# Revit family: Electronics_Expansion-Inputs_Biamp_Vocia_8-Channel-Live-Audio-Input-Device_VI-8__
name_source: partatom
category: Communication Devices
units: mm (PartAtom-declared; Revit-internal decimal feet)

## family parameters
Cut with Voids When Loaded = No
Host = Face
Maintain Annotation Orientation = No
OmniClass Number = 23.85.10.11.14
OmniClass Title = Audio Equipment
Part Type = Normal
Room Calculation Point = No
Round Connector Dimension = Use Diameter
Shared = No

## types (1)
- VI-8
    A/D Converters = 24-bit
    Altitude = 0-10,000 ft (0-3000m) MSL
    Apparent Load = 35 VA
    Compliance = FCC Part 15B (USA); CE marked (Europe); RCM (Australia); EAC (Eurasian Customs Union); RoHS Directive (Europe)
    Connector Description = 24V DC; <100mV Ripple (Max 35W)
    Crosstalk = 10kHz: < -75dB
    Current Limit = 0.8A
    DC Input = 24V DC; <100mV Ripple (Max 35W)
    DC Reference Output = 24V; 100mA limited
    Default Elevation = 4' - 0"
    Depth = 0' - 10"
    Description = Vocia® VI-8 8-Channel Live Audio Input Device
    Dynamic Range = >100dB
    Equivalent Input Noise = < -125dBu
    Frequency Response = 20Hz~20kHz: +0, -1dB
    Height = 0' - 1 1/2"
    High Range Logic High = 12-30V DC
    High Range Logic Low = 0-8V DC
    Housing Material = Biamp - Metal - Silver
    Humidity = 0-95% relative humidity (non-condensing)
    Input Impedance = 8kOhm
    Input Isolation = 500V RMS
    Input Transient Protection = ± 8kV Peak
    Manufacturer = Biamp
    Max Continuous Current = 0.35A
    Max Input Level = 24dBu
    Max Operating Voltage = 125VAC, 60VDC / 35V
    Max Power Consumption = 35 W
    Max Switching Capacity = 37VA
    Min Operating Load = 10μA at 10mV DC
    Model = Vocia VI-8
    Network Audio = 20-bits, 48kHz, 5-1/3ms (fixed)
    Network Connection = Dual RJ45 with shielded Ethernet (CAT5, CAT5e, CAT6, or CAT7)
    Number of Poles = 1
    Power Factor = 1
    Product Documentation Link = https://downloads.biamp.com
    Product Page URL = https://www.biamp.com
    Product data url = https://www.bimobject.com
    Quantity Control Inputs = 9
    Quantity Control Outputs = 4
    Sample Rate = 48kHz
    Status Out Type = FET Switch, open drain (low side driver)
    THD+N = 20Hz~20kHz: <0.05%
    TTL Logic High = 2-5V
    TTL Logic Low = 0–0.8V
    Temperature Range = 18 - 108° F (-8 – 42° C)
    Type Control Outputs = Form C Voltage free change over contact
    URL = https://www.biamp.com
    Voltage = 24 V
    Weight = 6.60 lbf
    Width = 1' - 7"

## geometry (parser evidence)
native form markers: Sweep x3
no freeform markers — native parametric forms only
